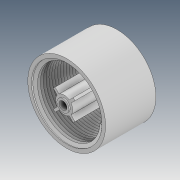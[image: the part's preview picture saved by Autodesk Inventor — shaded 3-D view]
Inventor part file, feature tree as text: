
AUTODESK INVENTOR PART (.ipt)
format: ipt  version: 2020 (Build 240168000, 168)  size: 468,480 bytes
history: native  units: mm
features: sketch x5, extrude x4, plane x1, helix x1, chamfer x1
ambient origin geometry x8: Origin, YZ Plane, XZ Plane, XY Plane, X Axis, Y Axis, Z Axis, Center Point
bodies: Solid1 (feature_tree)
feature tree (12):
  extrude  "Extrusion1"  Depth=1.6mm
  extrude  "Extrusion2"  Depth=8.0mm
  extrude  "Extrusion3"  Depth=40.0mm TaperAngle=360.0deg
  sketch  "Sketch4"  dims[d11=3.5mm d12=2.0mm d13=0.0mm d14=7.5mm]
  plane  "Work Plane1"
  extrude  "Extrusion4"  Depth=2.0mm TaperAngle=0.0deg
  helix  "Coil3"  [1 undecoded]
  chamfer  "Chamfer1"  Angle=45.0deg  [1 undecoded]
  sketch  "Sketch1"  dims[d1=30.8mm d2=1.6mm]
  sketch  "Sketch2"  dims[d3=20.0mm d4=0.0mm d5=8.0mm]
  sketch  "Sketch3"  dims[d6=8.0mm d7=40.0mm d9=360.0deg]
  sketch  "Sketch6"  dims[d15=1.11mm d16=45.0deg d17=1.11mm d18=45.0deg d19=12.33mm d20=12.33mm d21=21.11mm d22=0.0mm d45=-0.9mm d51=5.3mm d52=0.5mm d53=0.0mm d54=1.4mm d55=1.25mm d56=1.25mm d57=20.0mm d58=10.0mm d59=0.0mm d60=90.0deg d61=90.0deg d62=0.0mm d63=0.0mm d64=0.559mm d65=2.0mm d66=45.0deg]
note: 2 required parameter values undecoded (feature->parameter linkage not recoverable at this tier; creation-order binding heuristic only, values carry confidence <= 0.55)
